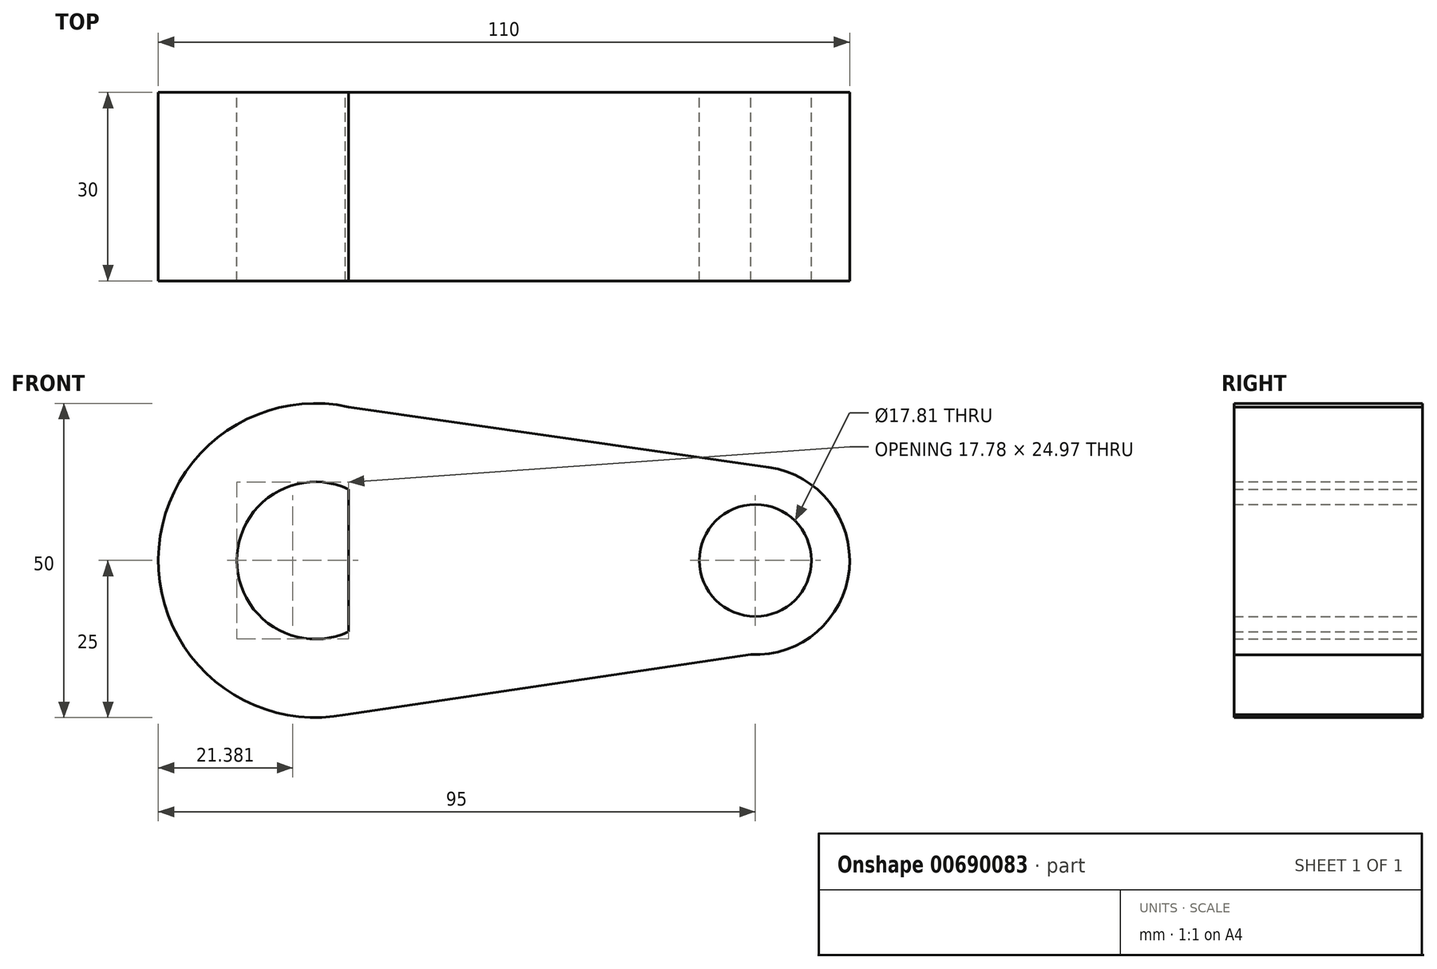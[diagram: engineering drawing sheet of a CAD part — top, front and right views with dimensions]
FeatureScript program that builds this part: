
annotation { "Feature Type Name" : "Feature", "Feature Type Description" : "" }
export const myFeature = defineFeature(function(context is Context, id is Id, definition is map)
    precondition{}
    {
        {
            var Q0;
            Q0=qCreatedBy(makeId("Front.planeOp"),FACE);
            var sketch = newSketch(context, id + "F0", { "sketchPlane" : qUnion([Q0])});
            skCircle(sketch, "E0", {"center": v(0, 0) * mm, "radius": 25 * mm});
            skCircle(sketch, "E1", {"center": v(70, 0) * mm, "radius": 15 * mm});
            skLineSegment(sketch, "E2", {"start": v(5.27, 24.44) * mm, "end": v(72.13, 14.85) * mm});
            skLineSegment(sketch, "E3", {"start": v(4.78, -24.54) * mm, "end": v(69.27, -14.98) * mm});
            skCircle(sketch, "E4", {"center": v(0, 0) * mm, "radius": 12.51 * mm});
            skCircle(sketch, "E5", {"center": v(70, 0) * mm, "radius": 8.9 * mm});
            skLineSegment(sketch, "E6", {"start": v(5.27, 11.35) * mm, "end": v(5.27, -11.35) * mm});
            skSolve(sketch);
        }
        {
            var Q0;
            Q0 = qSketchRegion(id + "F0", true);
            extrude(context, id + "F1", {"entities" : qUnion([Q0]), "depth" : 30 * mm, "offsetDistance" : 25 * mm});
        }
        {
            var Q0;
            {var subQ0=sQuery(id+"F0.wireOp",EDGE,"E6");Q0=makeQuery(id+"F0.imprint","IMPRINT",FACE,{"disambiguationData":[TD([[makeQuery(id+"F0.imprint","IMPRINT",EDGE,{"derivedFrom":subQ0}),1.0]])]});}
            extrude(context, id + "F2", {"entities" : qUnion([Q0]), "operationType" : NewBodyOperationType.ADD, "depth" : 30 * mm, "offsetDistance" : 25 * mm});
        }
    });
